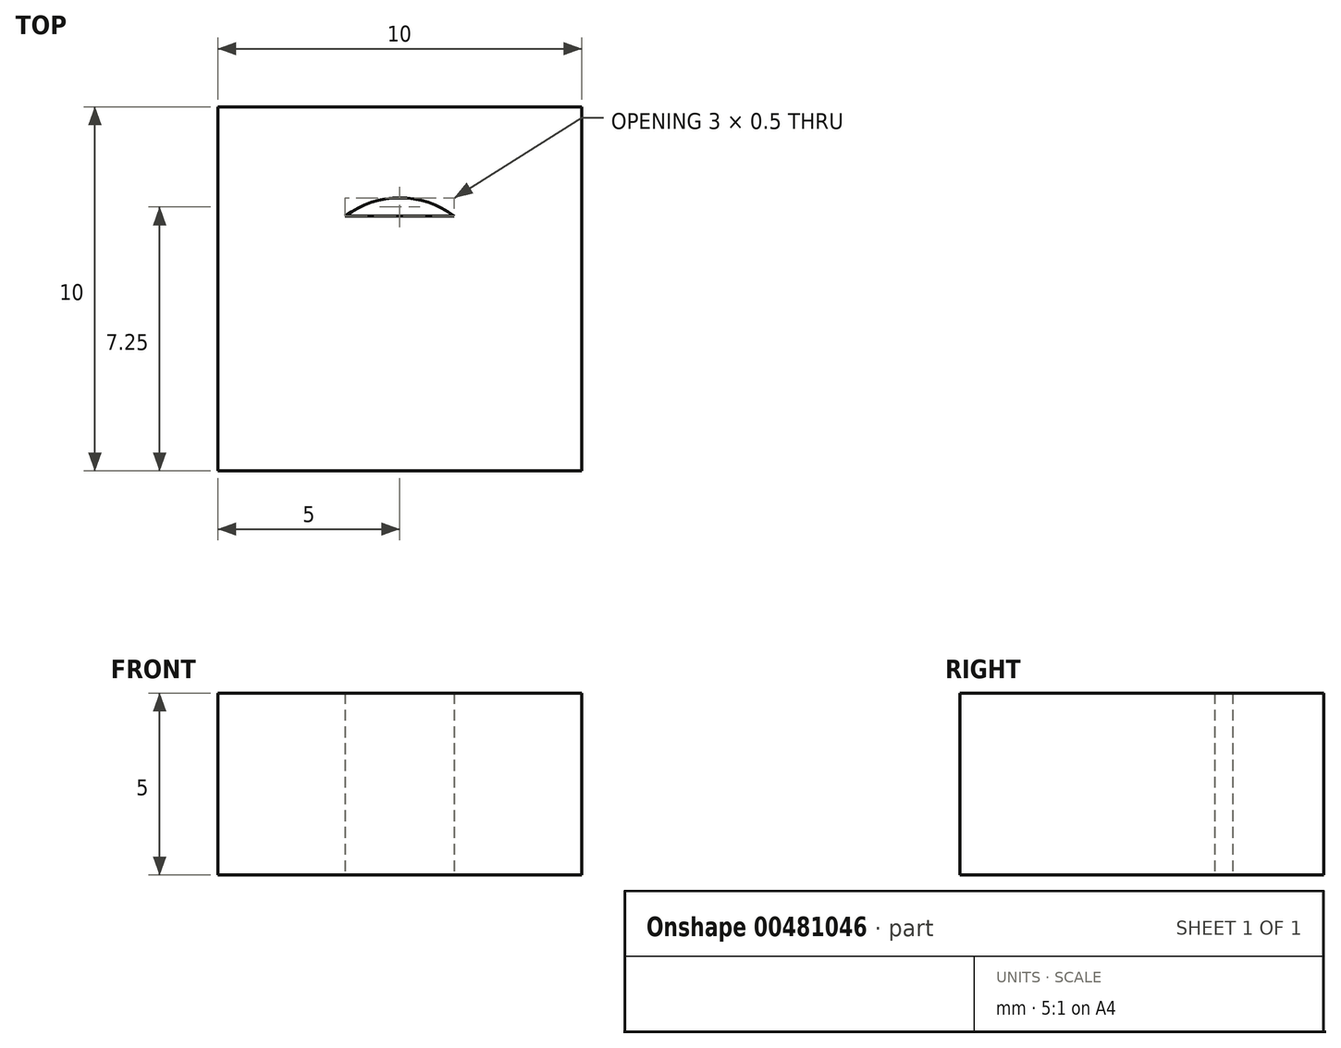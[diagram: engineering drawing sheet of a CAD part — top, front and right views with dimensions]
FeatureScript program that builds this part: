
annotation { "Feature Type Name" : "Feature", "Feature Type Description" : "" }
export const myFeature = defineFeature(function(context is Context, id is Id, definition is map)
    precondition{}
    {
        {
            var Q0;
            Q0=qCreatedBy(makeId("Top.planeOp"),FACE);
            var sketch = newSketch(context, id + "F0", { "sketchPlane" : qUnion([Q0])});
            skCircle(sketch, "E0", {"center": v(0, 0) * mm, "radius": 2.5 * mm});
            skLineSegment(sketch, "E1.bottom", {"start": v(-3.38, 4.88) * mm, "end": v(3.42, 4.88) * mm});
            skLineSegment(sketch, "E1.top", {"start": v(-3.38, 2) * mm, "end": v(3.42, 2) * mm});
            skLineSegment(sketch, "E1.left", {"start": v(-3.38, 4.88) * mm, "end": v(-3.38, 2) * mm});
            skLineSegment(sketch, "E1.right", {"start": v(3.42, 4.88) * mm, "end": v(3.42, 2) * mm});
            skLineSegment(sketch, "E2.bottom", {"start": v(5, -5) * mm, "end": v(-5, -5) * mm});
            skLineSegment(sketch, "E2.top", {"start": v(5, 5) * mm, "end": v(-5, 5) * mm});
            skLineSegment(sketch, "E2.left", {"start": v(5, -5) * mm, "end": v(5, 5) * mm});
            skLineSegment(sketch, "E2.right", {"start": v(-5, -5) * mm, "end": v(-5, 5) * mm});
            skSolve(sketch);
        }
        {
            var Q0;
            Q0=makeQuery(id+"F0.imprint","IMPRINT",FACE,{"disambiguationData":[TD([[makeQuery(id+"F0.imprint","IMPRINT",EDGE,{"derivedFrom":sQuery(id+"F0.wireOp",EDGE,"E1.bottom")}),1.0]])]});
            var Q1;
            Q1=makeQuery(id+"F0.imprint","IMPRINT",FACE,{"disambiguationData":[TD([[makeQuery(id+"F0.imprint","IMPRINT",EDGE,{"derivedFrom":sQuery(id+"F0.wireOp",EDGE,"E1.bottom")}),-1.0]])]});
            var Q2;
            {var subQ0=sQuery(id+"F0.wireOp",EDGE,"E1.top");var subQ1=sQuery(id+"F0.wireOp",EDGE,"E0");var subQ2=makeQuery(id+"F0.imprint","INTERSECT",VERTEX,{"disambiguationData":[OD(0.0)],"derivedFrom":[subQ1,subQ0]});Q2=makeQuery(id+"F0.imprint","IMPRINT",FACE,{"disambiguationData":[TD([[makeQuery(id+"F0.imprint","IMPRINT",EDGE,{"disambiguationData":[TD([[subQ2,1.0]])],"derivedFrom":subQ1}),1.0]])]});}
            extrude(context, id + "F1", {"entities" : qUnion([Q0, Q1, Q2]), "depth" : 5 * mm});
        }
    });
